# Revit family: Sanitary_Shower-screens_Duscholux_Pure-Style_Perseus_Two-fixed-segments+pivot-twin-doors-angle-acces-Shower
name_source: partatom
category: Plumbing Fixtures
revit_build: Autodesk Revit 2016 (Build: 20150220_1215(x64)
units: mm (PartAtom-declared; Revit-internal decimal feet)

## family parameters
Always vertical = Yes
Cut with Voids When Loaded = No
OmniClass Number = 23.45.00.00
OmniClass Title = Sanitary, Laundry, and Cleaning Equipment
Part Type = Normal
Room Calculation Point = No
Round Connector Dimension = Use Diameter
Shared = No
Work Plane-Based = No

## types (2) — shared parameters
Accesories Material = Chrome_Finish
Assembly Code = C1030200
Brand = Duscholux
Certified Quality UNE EN 14428 = http://www.duscholux.es
Combinations = Hinge and handle to choice (Round, square or triangular)
Components = Eropean components
Configuration enclosure = http://configuratumampara.duscholux.es
Description = 2 fixed segments + pivot twin doors at 180º with angle access for shower
Design country = Spain / Germany
Edition number = 1
Environmental Management ISO 14001 = ECOEMBES Certificate
Fact Sheet = http://blob.duscholux.es
Front door aperture = 720 mm  [stored 2.3622 ft]
Glass Material = Glass_Material-Duscholux
Glass in Building UNE EN 12150 = CE Conformity marking
Handle Height = 1000 mm  [stored 3.28084 ft]
Handle Material = Chrome_Finish
Height = 2000 mm  [stored 6.56168 ft]
IFC Classification = Furnishing Element
Image = https://www.duscholux.es
Lateral door aperture = 720 mm  [stored 2.3622 ft]
Maintenance and Cleaning = http://www.duscholux.es
Manufacturer = Duscholux Ibérica, S.A.
Manufacturer country = Spain
Manufacturer name = Duscholux Ibérica, S.A.
Max Height = 2000 mm  [stored 6.56168 ft]
Min Max Openning front angle = 0.00°
Min Max Openning lateral angle = 0.00°
Min Max Width front side = 900 mm  [stored 2.95276 ft]
Min Max Width lateral side = 900 mm  [stored 2.95276 ft]
Model = Perseus
NBS Reference Code = 45-35-70
NBS Reference Description = Shower Enclosures
Net Weight (Kg) = 83
Opening System = Pivot Door
Opening System Image = http://blob.duscholux.es
Openning front angle = 0.00°
Openning lateral angle = 0.00°
Product family = Pure Style
Product group = Front for shower
Products = http://www.duscholux.es
Series = Pure Style
Technical Inspection Certificate (Applus) = http://www.duscholux.es
Thickness Glass = 6 mm  [stored 0.019685 ft]
UNSPSC Code = 30181507
URL = http://www.duscholux.es
Uniclass 2015 Code = PR-40-20-06-79
Uniclass 2015 Description = Shower Enclosures
Width front fixed segment = 180 mm  [stored 0.590551 ft]
Width front side = 900 mm  [stored 2.95276 ft]
Width lateral fixed segment = 180 mm  [stored 0.590551 ft]
Width lateral side = 900 mm  [stored 2.95276 ft]

## per-type parameters (varying)
| type | Ref. |
| Silver Matt Aluminium Finish | 4UI / 4UD |
| Platinum Aluminium Finish | 4PF / 4PG |

note: column(s) folded — value = type name in every type: Frame Material

note: [stored X ft] marks values corroborated as IEEE doubles in the binary element streams (Revit-internal decimal feet)
